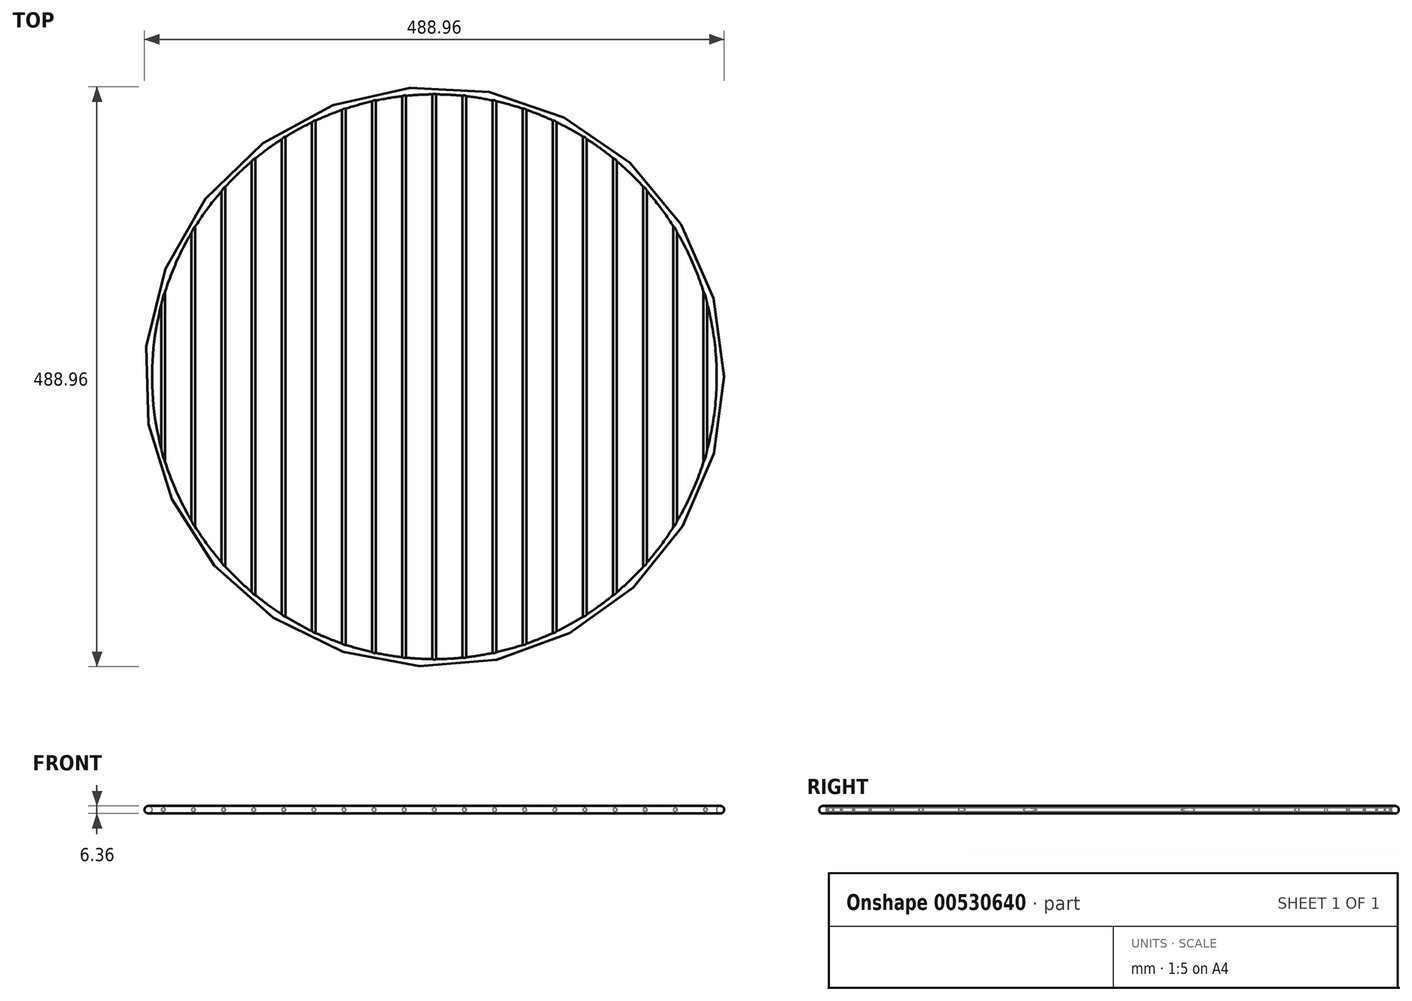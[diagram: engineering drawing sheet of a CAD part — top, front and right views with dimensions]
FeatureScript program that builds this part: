
annotation { "Feature Type Name" : "Feature", "Feature Type Description" : "" }
export const myFeature = defineFeature(function(context is Context, id is Id, definition is map)
    precondition{}
    {
        {
            var Q0;
            Q0=qCreatedBy(makeId("Front.planeOp"),FACE);
            var sketch = newSketch(context, id + "F0", { "sketchPlane" : qUnion([Q0])});
            skCircle(sketch, "E0", {"center": v(241.3, 0) * mm, "radius": 3.18 * mm});
            skLineSegment(sketch, "E1", {"start": v(0, 0) * mm, "end": v(0, 32.12) * mm, "construction": true});
            skSolve(sketch);
        }
        {
            var Q0;
            Q0 = qSketchRegion(id + "F0", true);
            var Q1;
            Q1=sQuery(id+"F0.wireOp",EDGE,"E1");
            revolve(context, id + "F1", {"entities" : qUnion([Q0]), "axis" : qUnion([Q1]), "revolveType" : RevolveType.FULL});
        }
        {
            var Q0;
            Q0=qCreatedBy(makeId("Front.planeOp"),FACE);
            var sketch = newSketch(context, id + "F2", { "sketchPlane" : qUnion([Q0])});
            skCircle(sketch, "E2", {"center": v(0, 0) * mm, "radius": 1.59 * mm});
            skCircle(sketch, "E3.1.0.0", {"center": v(25.4, 0) * mm, "radius": 1.59 * mm});
            skCircle(sketch, "E3.2.0.0", {"center": v(50.8, 0) * mm, "radius": 1.59 * mm});
            skLineSegment(sketch, "E3.direction1", {"start": v(0, 0) * mm, "end": v(25.4, 0) * mm, "construction": true});
            skCircle(sketch, "E4.0.3.0", {"center": v(76.2, 0) * mm, "radius": 1.59 * mm});
            skCircle(sketch, "E4.0.4.0", {"center": v(101.6, 0) * mm, "radius": 1.59 * mm});
            skCircle(sketch, "E5.0.5.0", {"center": v(127, 0) * mm, "radius": 1.59 * mm});
            skCircle(sketch, "E5.0.6.0", {"center": v(152.4, 0) * mm, "radius": 1.59 * mm});
            skCircle(sketch, "E5.0.7.0", {"center": v(177.8, 0) * mm, "radius": 1.59 * mm});
            skCircle(sketch, "E5.0.8.0", {"center": v(203.2, 0) * mm, "radius": 1.59 * mm});
            skCircle(sketch, "E5.0.9.0", {"center": v(228.6, 0) * mm, "radius": 1.59 * mm});
            skCircle(sketch, "E6.1.0.0", {"center": v(-25.4, 0) * mm, "radius": 1.59 * mm});
            skCircle(sketch, "E6.2.0.0", {"center": v(-50.8, 0) * mm, "radius": 1.59 * mm});
            skCircle(sketch, "E6.3.0.0", {"center": v(-76.2, 0) * mm, "radius": 1.59 * mm});
            skCircle(sketch, "E6.4.0.0", {"center": v(-101.6, 0) * mm, "radius": 1.59 * mm});
            skCircle(sketch, "E6.5.0.0", {"center": v(-127, 0) * mm, "radius": 1.59 * mm});
            skCircle(sketch, "E6.6.0.0", {"center": v(-152.4, 0) * mm, "radius": 1.59 * mm});
            skCircle(sketch, "E6.7.0.0", {"center": v(-177.8, 0) * mm, "radius": 1.59 * mm});
            skCircle(sketch, "E6.8.0.0", {"center": v(-203.2, 0) * mm, "radius": 1.59 * mm});
            skCircle(sketch, "E6.9.0.0", {"center": v(-228.6, 0) * mm, "radius": 1.59 * mm});
            skLineSegment(sketch, "E6.direction1", {"start": v(0, 0) * mm, "end": v(-25.4, 0) * mm, "construction": true});
            skSolve(sketch);
        }
        {
            var Q0;
            Q0 = qSketchRegion(id + "F2", true);
            extrude(context, id + "F3", {"entities" : qUnion([Q0]), "operationType" : NewBodyOperationType.ADD, "endBound" : BoundingType.UP_TO_NEXT, "depth" : 25.4 * mm, "offsetDistance" : 25.4 * mm, "hasSecondDirection" : true, "secondDirectionBound" : SecondDirectionBoundingType.UP_TO_NEXT, "secondDirectionOppositeDirection" : true, "secondDirectionDepth" : 25.4 * mm});
        }
    });
